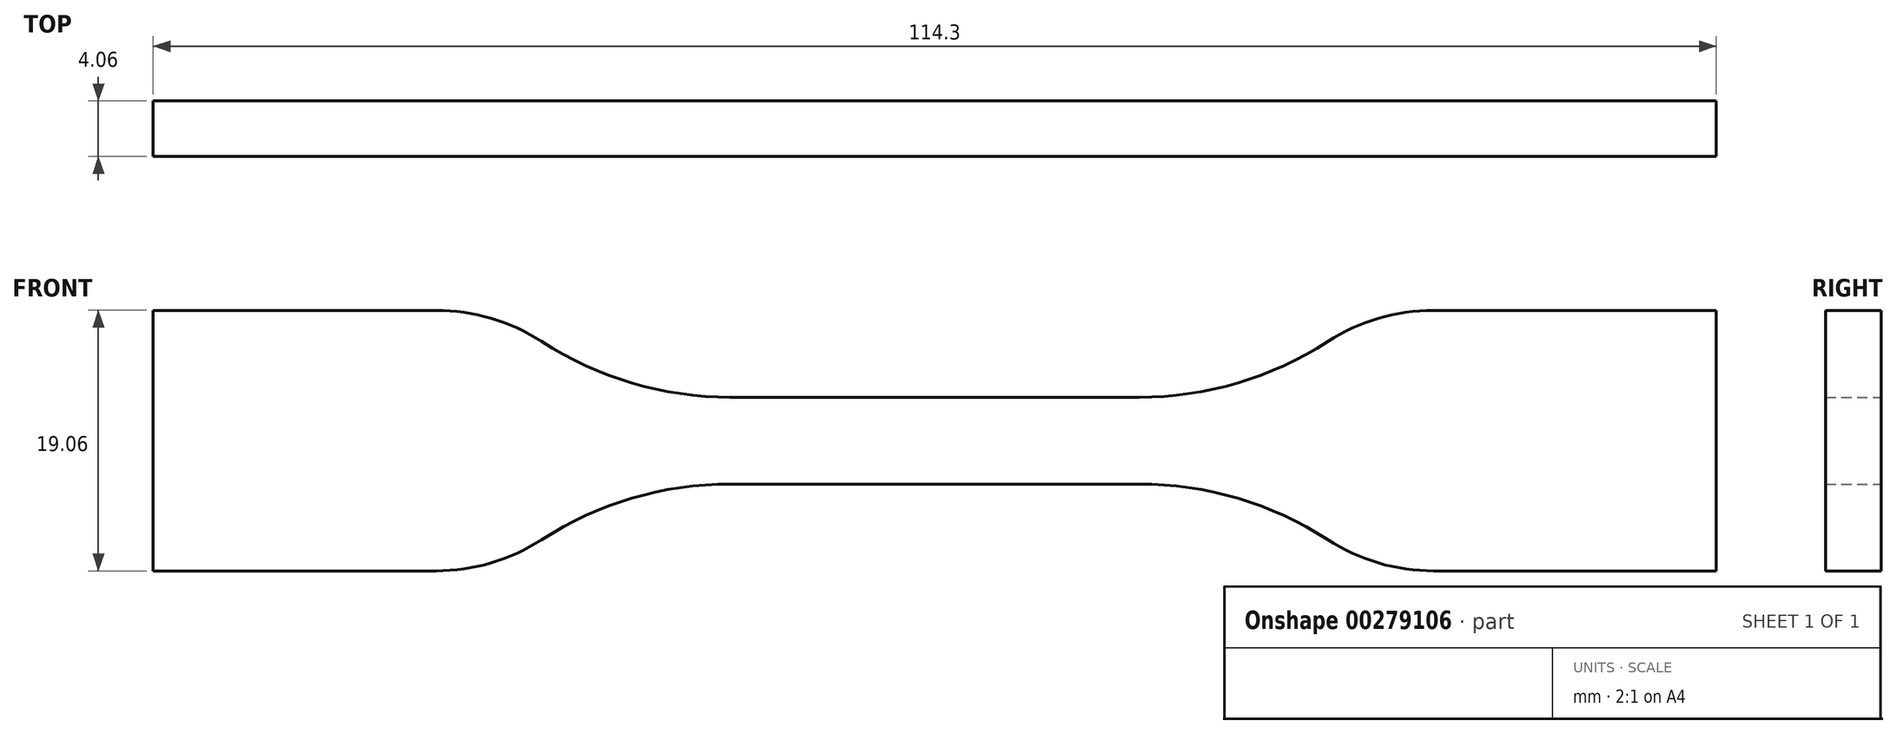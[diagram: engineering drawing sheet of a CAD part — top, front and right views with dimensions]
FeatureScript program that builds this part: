
annotation { "Feature Type Name" : "Feature", "Feature Type Description" : "" }
export const myFeature = defineFeature(function(context is Context, id is Id, definition is map)
    precondition{}
    {
        {
            var Q0;
            Q0=qCreatedBy(makeId("Front.planeOp"),FACE);
            var sketch = newSketch(context, id + "F0", { "sketchPlane" : qUnion([Q0])});
            skLineSegment(sketch, "E0", {"start": v(0, 3.18) * mm, "end": v(14.95, 3.18) * mm});
            skArc(sketch, "E1", {"start": v(14.95, 3.18) * mm, "mid": v(22.14, 4.21) * mm, "end": v(28.74, 7.25) * mm});
            skLineSegment(sketch, "E2", {"start": v(36.46, 9.53) * mm, "end": v(57.15, 9.53) * mm});
            skLineSegment(sketch, "E3", {"start": v(57.15, 9.53) * mm, "end": v(57.15, 0) * mm});
            skLineSegment(sketch, "E4.MirrorCS", {"start": v(0, -3.17) * mm, "end": v(14.95, -3.17) * mm});
            skLineSegment(sketch, "E5.MirrorCS", {"start": v(57.15, -9.53) * mm, "end": v(57.15, 0) * mm});
            skLineSegment(sketch, "E6.MirrorCS", {"start": v(36.46, -9.53) * mm, "end": v(57.15, -9.53) * mm});
            skArc(sketch, "E7.MirrorCS", {"start": v(14.95, -3.18) * mm, "mid": v(22.14, -4.21) * mm, "end": v(28.74, -7.25) * mm});
            skArc(sketch, "E8.MirrorCS", {"start": v(-14.95, -3.18) * mm, "mid": v(-22.14, -4.21) * mm, "end": v(-28.74, -7.25) * mm});
            skLineSegment(sketch, "E9.MirrorCS", {"start": v(-36.46, -9.53) * mm, "end": v(-57.15, -9.53) * mm});
            skArc(sketch, "E10.MirrorCS", {"start": v(-14.95, 3.18) * mm, "mid": v(-22.14, 4.21) * mm, "end": v(-28.74, 7.25) * mm});
            skLineSegment(sketch, "E11.MirrorCS", {"start": v(-36.46, 9.53) * mm, "end": v(-57.15, 9.53) * mm});
            skLineSegment(sketch, "E12.MirrorCS", {"start": v(-57.15, -9.53) * mm, "end": v(-57.15, 0) * mm});
            skLineSegment(sketch, "E13.MirrorCS", {"start": v(0, -3.17) * mm, "end": v(-14.95, -3.17) * mm});
            skLineSegment(sketch, "E14.MirrorCS", {"start": v(-57.15, 9.53) * mm, "end": v(-57.15, 0) * mm});
            skLineSegment(sketch, "E15.MirrorCS", {"start": v(0, 3.18) * mm, "end": v(-14.95, 3.18) * mm});
            skPoint(sketch, "E16.visualSharp", {"position": v(31.75, 9.52) * mm});
            skArc(sketch, "E16.filletArc", {"start": v(36.46, 9.53) * mm, "mid": v(32.44, 8.94) * mm, "end": v(28.74, 7.25) * mm});
            skPoint(sketch, "E17.visualSharp", {"position": v(31.75, -9.53) * mm});
            skArc(sketch, "E17.filletArc", {"start": v(28.74, -7.25) * mm, "mid": v(32.44, -8.94) * mm, "end": v(36.46, -9.53) * mm});
            skPoint(sketch, "E18.visualSharp", {"position": v(-31.75, 9.52) * mm});
            skArc(sketch, "E18.filletArc", {"start": v(-28.74, 7.25) * mm, "mid": v(-32.44, 8.94) * mm, "end": v(-36.46, 9.53) * mm});
            skPoint(sketch, "E19.visualSharp", {"position": v(-31.75, -9.52) * mm});
            skArc(sketch, "E19.filletArc", {"start": v(-36.46, -9.53) * mm, "mid": v(-32.44, -8.94) * mm, "end": v(-28.74, -7.25) * mm});
            skSolve(sketch);
        }
        {
            var Q0;
            Q0 = qSketchRegion(id + "F0", true);
            extrude(context, id + "F1", {"entities" : qUnion([Q0]), "depth" : 4.06 * mm});
        }
    });
